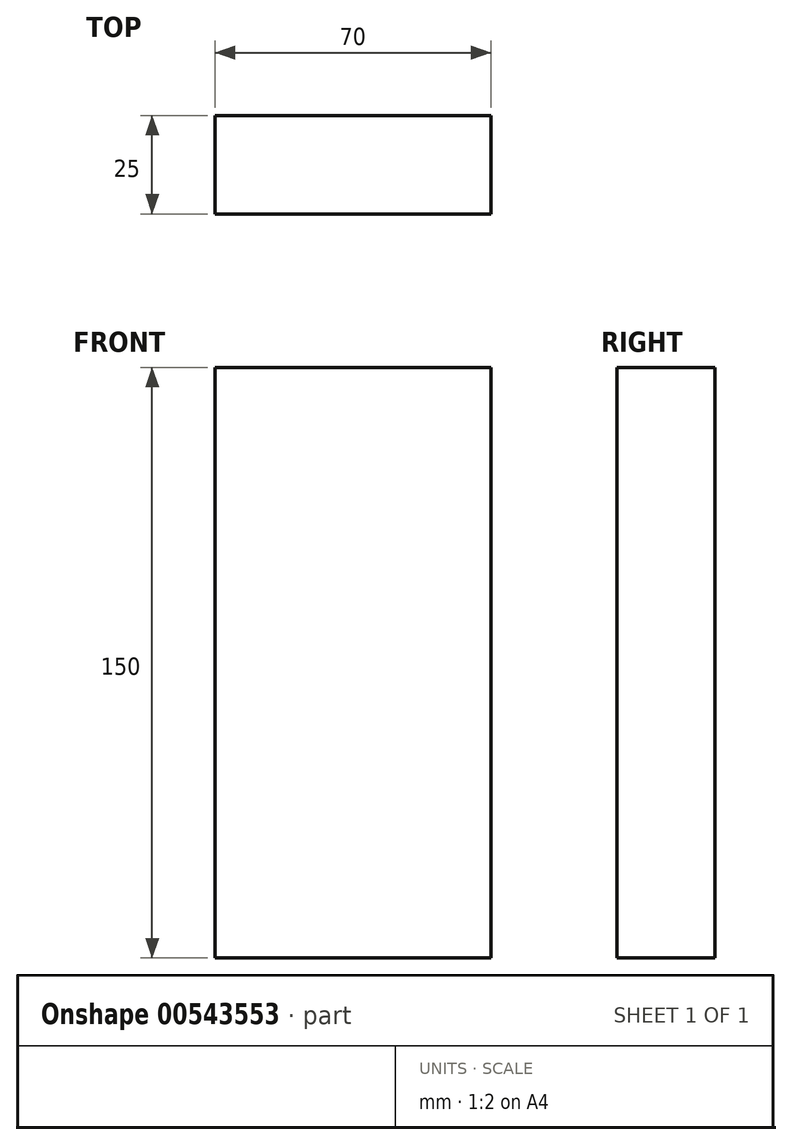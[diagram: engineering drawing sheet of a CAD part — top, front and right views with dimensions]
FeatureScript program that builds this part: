
annotation { "Feature Type Name" : "Feature", "Feature Type Description" : "" }
export const myFeature = defineFeature(function(context is Context, id is Id, definition is map)
    precondition{}
    {
        {
            var Q0;
            Q0=qCreatedBy(makeId("Front.planeOp"),FACE);
            var sketch = newSketch(context, id + "F0", { "sketchPlane" : qUnion([Q0])});
            skLineSegment(sketch, "E0.bottom", {"start": v(-35, -75) * mm, "end": v(35, -75) * mm});
            skLineSegment(sketch, "E0.top", {"start": v(-35, 75) * mm, "end": v(35, 75) * mm});
            skLineSegment(sketch, "E0.left", {"start": v(-35, -75) * mm, "end": v(-35, 75) * mm});
            skLineSegment(sketch, "E0.right", {"start": v(35, -75) * mm, "end": v(35, 75) * mm});
            skPoint(sketch, "E0.middle", {"position": v(0, 0) * mm});
            skLineSegment(sketch, "E1.bottom", {"start": v(35, -75) * mm, "end": v(34.2, -75) * mm});
            skLineSegment(sketch, "E1.top", {"start": v(35, 75) * mm, "end": v(34.2, 75) * mm});
            skLineSegment(sketch, "E1.right", {"start": v(34.2, -75) * mm, "end": v(34.2, 75) * mm});
            skSolve(sketch);
        }
        {
            var Q0;
            Q0=makeQuery(id+"F0.imprint","IMPRINT",FACE,{"disambiguationData":[TD([[makeQuery(id+"F0.imprint","IMPRINT",EDGE,{"derivedFrom":sQuery(id+"F0.wireOp",EDGE,"E0.bottom")}),1.0]])]});
            extrude(context, id + "F1", {"entities" : qUnion([Q0]), "depth" : 25 * mm, "offsetDistance" : 25 * mm});
        }
    });
